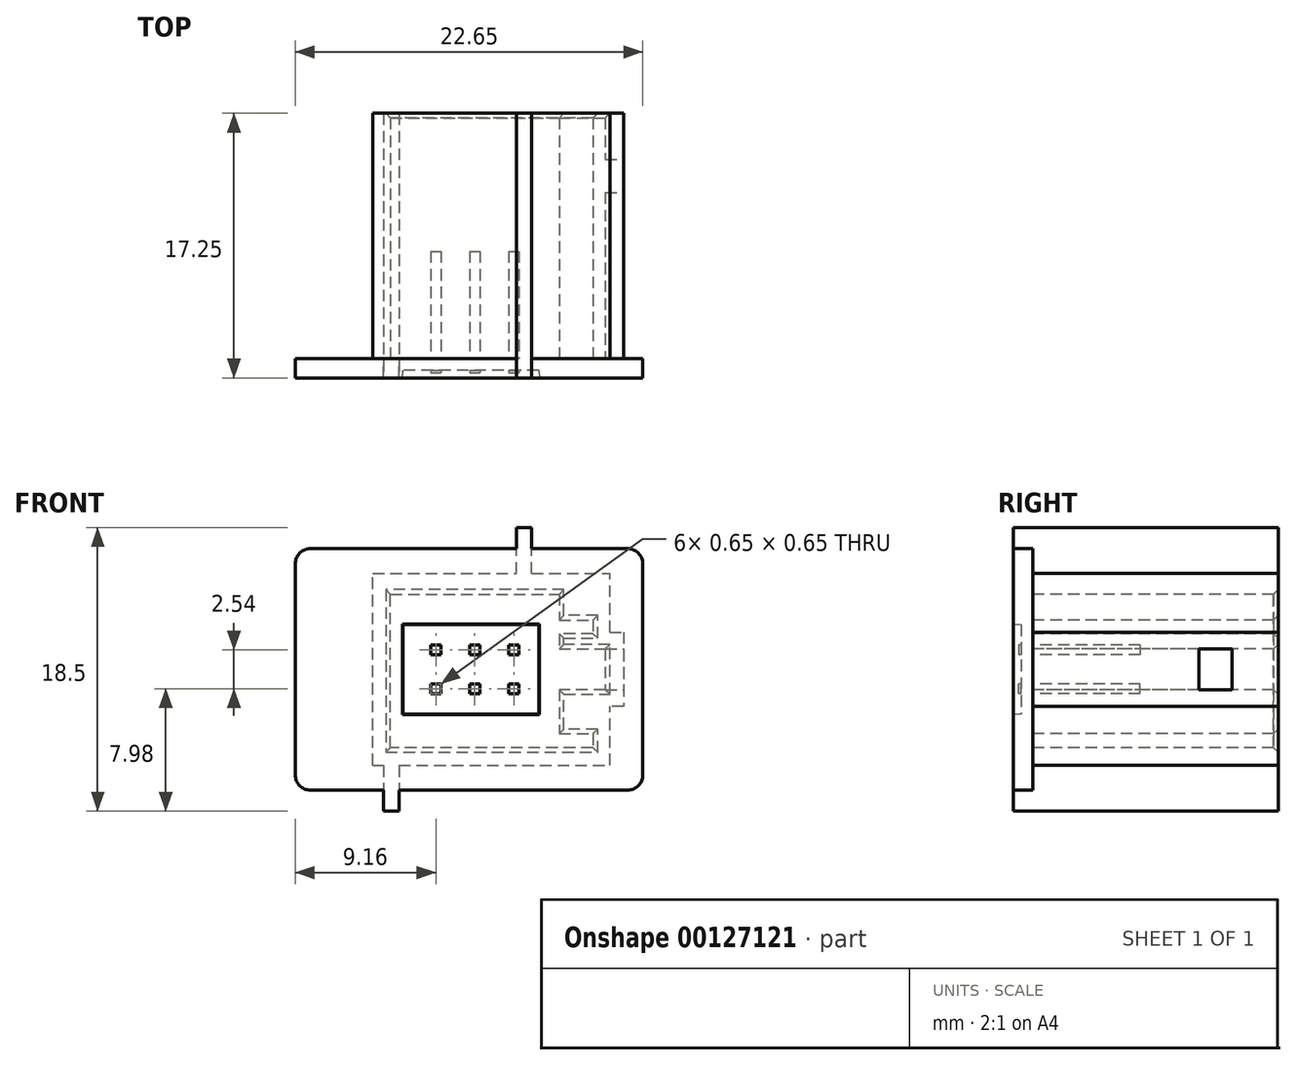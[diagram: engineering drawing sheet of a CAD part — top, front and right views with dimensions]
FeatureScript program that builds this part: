
annotation { "Feature Type Name" : "Feature", "Feature Type Description" : "" }
export const myFeature = defineFeature(function(context is Context, id is Id, definition is map)
    precondition{}
    {
        {
            var Q0;
            Q0=qCreatedBy(makeId("Front.planeOp"),FACE);
            var sketch = newSketch(context, id + "F0", { "sketchPlane" : qUnion([Q0])});
            skLineSegment(sketch, "E0", {"start": v(0, 0) * mm, "end": v(0, 10) * mm});
            skLineSegment(sketch, "E1", {"start": v(0, 10) * mm, "end": v(11, 10) * mm});
            skLineSegment(sketch, "E2", {"start": v(13.2, 8.32) * mm, "end": v(13.2, 7.42) * mm});
            skLineSegment(sketch, "E3", {"start": v(13.2, 7.42) * mm, "end": v(11, 7.42) * mm});
            skLineSegment(sketch, "E4", {"start": v(11, 7.42) * mm, "end": v(11, 6.42) * mm});
            skLineSegment(sketch, "E5", {"start": v(11, 6.42) * mm, "end": v(14, 6.42) * mm});
            skLineSegment(sketch, "E6", {"start": v(14, 6.43) * mm, "end": v(14, 3.77) * mm});
            skLineSegment(sketch, "E7", {"start": v(14, 3.77) * mm, "end": v(11, 3.77) * mm});
            skLineSegment(sketch, "E8", {"start": v(11, 3.77) * mm, "end": v(11, 0.9) * mm});
            skLineSegment(sketch, "E9", {"start": v(11, 0.9) * mm, "end": v(13.2, 0.9) * mm});
            skLineSegment(sketch, "E10", {"start": v(13.2, 0.9) * mm, "end": v(13.2, 0) * mm});
            skLineSegment(sketch, "E11", {"start": v(13.2, 0) * mm, "end": v(0, 0) * mm});
            skLineSegment(sketch, "E12.bottom", {"start": v(-1.15, -1.15) * mm, "end": v(-0.45, -1.15) * mm});
            skLineSegment(sketch, "E12.top", {"start": v(-1.15, 11.35) * mm, "end": v(8.2, 11.35) * mm});
            skLineSegment(sketch, "E12.left", {"start": v(-1.15, -1.15) * mm, "end": v(-1.15, 11.35) * mm});
            skLineSegment(sketch, "E12.right", {"start": v(14.3, -1.15) * mm, "end": v(14.3, 2.68) * mm});
            skLineSegment(sketch, "E13", {"start": v(14.3, 7.53) * mm, "end": v(15.2, 7.53) * mm});
            skLineSegment(sketch, "E14", {"start": v(15.2, 7.53) * mm, "end": v(15.2, 2.68) * mm});
            skLineSegment(sketch, "E15", {"start": v(15.2, 2.68) * mm, "end": v(14.3, 2.68) * mm});
            skLineSegment(sketch, "E16.top", {"start": v(8.2, 14.35) * mm, "end": v(9.2, 14.35) * mm});
            skLineSegment(sketch, "E16.left", {"start": v(8.2, 11.35) * mm, "end": v(8.2, 14.35) * mm});
            skLineSegment(sketch, "E16.right", {"start": v(9.2, 11.35) * mm, "end": v(9.2, 14.35) * mm});
            skLineSegment(sketch, "E17.top", {"start": v(0.55, -4.15) * mm, "end": v(-0.45, -4.15) * mm});
            skLineSegment(sketch, "E17.left", {"start": v(0.55, -1.15) * mm, "end": v(0.55, -4.15) * mm});
            skLineSegment(sketch, "E17.right", {"start": v(-0.45, -1.15) * mm, "end": v(-0.45, -4.15) * mm});
            skLineSegment(sketch, "E18.trimOffspring", {"start": v(9.2, 11.35) * mm, "end": v(14.3, 11.35) * mm});
            skLineSegment(sketch, "E19.trimOffspring", {"start": v(0.55, -1.15) * mm, "end": v(14.3, -1.15) * mm});
            skLineSegment(sketch, "E20.trimOffspring", {"start": v(14.3, 7.53) * mm, "end": v(14.3, 11.35) * mm});
            skLineSegment(sketch, "E21", {"start": v(15.2, 5.1) * mm, "end": v(-1.15, 5.1) * mm, "construction": true});
            skPoint(sketch, "E22", {"position": v(14, 5.1) * mm});
            skLineSegment(sketch, "E23.bottom", {"start": v(-6.2, 12.97) * mm, "end": v(16.45, 12.97) * mm});
            skLineSegment(sketch, "E23.top", {"start": v(-6.2, -2.78) * mm, "end": v(16.45, -2.78) * mm});
            skLineSegment(sketch, "E23.left", {"start": v(-6.2, 12.97) * mm, "end": v(-6.2, -2.77) * mm});
            skLineSegment(sketch, "E23.right", {"start": v(16.45, 12.97) * mm, "end": v(16.45, -2.78) * mm});
            skLineSegment(sketch, "E24", {"start": v(15.2, 5.1) * mm, "end": v(16.45, 5.1) * mm, "construction": true});
            skLineSegment(sketch, "E25.bottom", {"start": v(2.63, 6.7) * mm, "end": v(3.28, 6.7) * mm});
            skLineSegment(sketch, "E25.top", {"start": v(2.63, 6.05) * mm, "end": v(3.28, 6.05) * mm});
            skLineSegment(sketch, "E25.left", {"start": v(2.63, 6.7) * mm, "end": v(2.63, 6.04) * mm});
            skLineSegment(sketch, "E25.right", {"start": v(3.28, 6.7) * mm, "end": v(3.28, 6.05) * mm});
            skPoint(sketch, "E26", {"position": v(2.63, 6.37) * mm});
            skLineSegment(sketch, "E27.1.0.0", {"start": v(5.17, 6.05) * mm, "end": v(5.82, 6.05) * mm});
            skLineSegment(sketch, "E27.1.0.1", {"start": v(5.17, 6.7) * mm, "end": v(5.17, 6.04) * mm});
            skLineSegment(sketch, "E27.1.0.2", {"start": v(5.17, 6.7) * mm, "end": v(5.82, 6.7) * mm});
            skLineSegment(sketch, "E27.1.0.3", {"start": v(5.82, 6.7) * mm, "end": v(5.82, 6.05) * mm});
            skLineSegment(sketch, "E27.2.0.0", {"start": v(7.71, 6.05) * mm, "end": v(8.36, 6.05) * mm});
            skLineSegment(sketch, "E27.2.0.1", {"start": v(7.71, 6.7) * mm, "end": v(7.71, 6.04) * mm});
            skLineSegment(sketch, "E27.2.0.2", {"start": v(7.71, 6.7) * mm, "end": v(8.36, 6.7) * mm});
            skLineSegment(sketch, "E27.2.0.3", {"start": v(8.36, 6.7) * mm, "end": v(8.36, 6.05) * mm});
            skLineSegment(sketch, "E27.direction1", {"start": v(3.28, 6.05) * mm, "end": v(5.82, 6.05) * mm, "construction": true});
            skLineSegment(sketch, "E28.MirrorCS", {"start": v(2.63, 4.16) * mm, "end": v(3.28, 4.16) * mm});
            skLineSegment(sketch, "E29.MirrorCS", {"start": v(2.63, 3.5) * mm, "end": v(2.63, 4.16) * mm});
            skLineSegment(sketch, "E30.MirrorCS", {"start": v(2.63, 3.5) * mm, "end": v(3.28, 3.5) * mm});
            skLineSegment(sketch, "E31.MirrorCS", {"start": v(3.28, 3.5) * mm, "end": v(3.28, 4.16) * mm});
            skLineSegment(sketch, "E32.1.0.0", {"start": v(5.17, 3.5) * mm, "end": v(5.83, 3.5) * mm});
            skLineSegment(sketch, "E32.1.0.1", {"start": v(5.83, 3.5) * mm, "end": v(5.83, 4.16) * mm});
            skLineSegment(sketch, "E32.1.0.2", {"start": v(5.17, 4.16) * mm, "end": v(5.82, 4.16) * mm});
            skLineSegment(sketch, "E32.1.0.3", {"start": v(5.17, 3.5) * mm, "end": v(5.17, 4.16) * mm});
            skLineSegment(sketch, "E32.2.0.0", {"start": v(7.71, 3.5) * mm, "end": v(8.36, 3.5) * mm});
            skLineSegment(sketch, "E32.2.0.1", {"start": v(8.36, 3.5) * mm, "end": v(8.36, 4.16) * mm});
            skLineSegment(sketch, "E32.2.0.2", {"start": v(7.71, 4.16) * mm, "end": v(8.36, 4.16) * mm});
            skLineSegment(sketch, "E32.2.0.3", {"start": v(7.71, 3.5) * mm, "end": v(7.71, 4.16) * mm});
            skLineSegment(sketch, "E32.direction1", {"start": v(3.28, 4.16) * mm, "end": v(5.82, 4.16) * mm, "construction": true});
            skLineSegment(sketch, "E33", {"start": v(5.5, 0) * mm, "end": v(5.5, 10) * mm, "construction": true});
            skPoint(sketch, "E34", {"position": v(5.5, 3.5) * mm});
            skLineSegment(sketch, "E35", {"start": v(11, 10) * mm, "end": v(11, 8.32) * mm});
            skLineSegment(sketch, "E36", {"start": v(11, 8.32) * mm, "end": v(13.2, 8.32) * mm});
            skSolve(sketch);
        }
        {
            var Q0;
            Q0=makeQuery(id+"F0.imprint","IMPRINT",FACE,{"disambiguationData":[TD([[makeQuery(id+"F0.imprint","IMPRINT",EDGE,{"derivedFrom":sQuery(id+"F0.wireOp",EDGE,"E0")}),1.0]])]});
            var Q1;
            {var subQ0=sQuery(id+"F0.wireOp",EDGE,"E16.top");Q1=makeQuery(id+"F0.imprint","IMPRINT",FACE,{"disambiguationData":[TD([[makeQuery(id+"F0.imprint","IMPRINT",EDGE,{"derivedFrom":subQ0}),-1.0]])]});}
            var Q2;
            {var subQ0=sQuery(id+"F0.wireOp",EDGE,"E17.top");Q2=makeQuery(id+"F0.imprint","IMPRINT",FACE,{"disambiguationData":[TD([[makeQuery(id+"F0.imprint","IMPRINT",EDGE,{"derivedFrom":subQ0}),-1.0]])]});}
            extrude(context, id + "F1", {"entities" : qUnion([Q0, Q1, Q2]), "oppositeDirection" : true, "depth" : 16 * mm});
        }
        {
            var Q0;
            Q0 = qSketchRegion(id + "F0", true);
            var Q1;
            Q1=makeQuery(id+"F0.imprint","IMPRINT",FACE,{"disambiguationData":[TD([[makeQuery(id+"F0.imprint","IMPRINT",EDGE,{"derivedFrom":sQuery(id+"F0.wireOp",EDGE,"E0")}),-1.0]])]});
            extrude(context, id + "F2", {"entities" : qUnion([Q0, Q1]), "operationType" : NewBodyOperationType.ADD, "depth" : 1.25 * mm});
        }
        {
            var Q0;
            Q0=makeQuery(id+"F1.opExtrude","SWEPT_FACE",FACE,{"disambiguationData":[OSD([sQuery(id+"F0.wireOp",EDGE,"E14")])]});
            var sketch = newSketch(context, id + "F3", { "sketchPlane" : qUnion([Q0])});
            skLineSegment(sketch, "E37.bottom", {"start": v(10.85, 6.42) * mm, "end": v(13, 6.42) * mm});
            skLineSegment(sketch, "E37.top", {"start": v(10.85, 3.77) * mm, "end": v(13, 3.77) * mm});
            skLineSegment(sketch, "E37.left", {"start": v(10.85, 6.42) * mm, "end": v(10.85, 3.77) * mm});
            skLineSegment(sketch, "E37.right", {"start": v(13, 6.42) * mm, "end": v(13, 3.77) * mm});
            skLineSegment(sketch, "E38", {"start": v(16, 5.1) * mm, "end": v(0, 5.1) * mm, "construction": true});
            skPoint(sketch, "E39", {"position": v(13, 5.1) * mm});
            skLineSegment(sketch, "E40.0", {"start": v(16, 3.77) * mm, "end": v(0, 3.77) * mm, "construction": true});
            skSolve(sketch);
        }
        {
            var Q0;
            Q0=makeQuery(id+"F3.imprint","IMPRINT",FACE,{"disambiguationData":[TD([[makeQuery(id+"F3.imprint","IMPRINT",EDGE,{"derivedFrom":sQuery(id+"F3.wireOp",EDGE,"E37.bottom")}),-1.0]])]});
            var Q1;
            Q1=makeQuery(id+"F1.opExtrude","SWEPT_FACE",FACE,{"disambiguationData":[OSD([sQuery(id+"F0.wireOp",EDGE,"E6")])]});
            extrude(context, id + "F4", {"entities" : qUnion([Q0]), "operationType" : NewBodyOperationType.REMOVE, "endBound" : BoundingType.UP_TO_SURFACE, "oppositeDirection" : true, "endBoundEntityFace" : qUnion([Q1]), "depth" : 25 * mm});
        }
        {
            var Q0;
            Q0=makeQuery(id+"F2.opExtrude","SWEPT_EDGE",EDGE,{"disambiguationData":[OSD([sQuery(id+"F0.wireOp",EDGE,"E23.bottom"),sQuery(id+"F0.wireOp",EDGE,"E23.right")])]});
            var Q1;
            Q1=makeQuery(id+"F2.opExtrude","SWEPT_EDGE",EDGE,{"disambiguationData":[OSD([sQuery(id+"F0.wireOp",EDGE,"E23.bottom"),sQuery(id+"F0.wireOp",EDGE,"E23.left")])]});
            var Q2;
            Q2=makeQuery(id+"F2.opExtrude","SWEPT_EDGE",EDGE,{"disambiguationData":[OSD([sQuery(id+"F0.wireOp",EDGE,"E23.top"),sQuery(id+"F0.wireOp",EDGE,"E23.right")])]});
            var Q3;
            Q3=makeQuery(id+"F2.opExtrude","SWEPT_EDGE",EDGE,{"disambiguationData":[OSD([sQuery(id+"F0.wireOp",EDGE,"E23.top"),sQuery(id+"F0.wireOp",EDGE,"E23.left")])]});
            fillet(context, id + "F5", {"entities" : qUnion([Q0, Q1, Q2, Q3]), "radius" : 1 * mm, "tangentPropagation" : true, "allowEdgeOverflow" : false});
        }
        {
            var Q0;
            Q0=makeQuery(id+"F2.opExtrude","CAP_FACE",FACE,{"disambiguationData":[OSD([sQuery(id+"F0.wireOp",EDGE,"E16.top"),sQuery(id+"F0.wireOp",EDGE,"E16.left"),sQuery(id+"F0.wireOp",EDGE,"E16.right"),sQuery(id+"F0.wireOp",EDGE,"E17.top"),sQuery(id+"F0.wireOp",EDGE,"E17.left"),sQuery(id+"F0.wireOp",EDGE,"E17.right"),sQuery(id+"F0.wireOp",EDGE,"E23.bottom"),sQuery(id+"F0.wireOp",EDGE,"E23.top"),sQuery(id+"F0.wireOp",EDGE,"E23.left"),sQuery(id+"F0.wireOp",EDGE,"E23.right")])],"isStart":false});
            var sketch = newSketch(context, id + "F6", { "sketchPlane" : qUnion([Q0])});
            skLineSegment(sketch, "E41.bottom", {"start": v(0.8, 8.05) * mm, "end": v(9.7, 8.05) * mm});
            skLineSegment(sketch, "E41.top", {"start": v(0.8, 2.15) * mm, "end": v(9.7, 2.15) * mm});
            skLineSegment(sketch, "E41.left", {"start": v(0.8, 8.05) * mm, "end": v(0.8, 2.15) * mm});
            skLineSegment(sketch, "E41.right", {"start": v(9.7, 8.05) * mm, "end": v(9.7, 2.15) * mm});
            skLineSegment(sketch, "E42", {"start": v(0.8, 5.1) * mm, "end": v(-6.2, 5.1) * mm, "construction": true});
            skSolve(sketch);
        }
        {
            var Q0;
            Q0 = qSketchRegion(id + "F6", true);
            extrude(context, id + "F7", {"entities" : qUnion([Q0]), "operationType" : NewBodyOperationType.REMOVE, "oppositeDirection" : true, "depth" : 0.5 * mm, "hasDraft" : true, "draftAngle" : 3 * degree, "draftPullDirection" : true});
        }
        {
            var Q0;
            Q0=makeQuery(id+"F0.imprint","IMPRINT",FACE,{"disambiguationData":[TD([[makeQuery(id+"F0.imprint","IMPRINT",EDGE,{"derivedFrom":sQuery(id+"F0.wireOp",EDGE,"E25.bottom")}),-1.0]])]});
            var Q1;
            Q1=makeQuery(id+"F0.imprint","IMPRINT",FACE,{"disambiguationData":[TD([[makeQuery(id+"F0.imprint","IMPRINT",EDGE,{"derivedFrom":sQuery(id+"F0.wireOp",EDGE,"E27.1.0.0")}),1.0]])]});
            var Q2;
            Q2=makeQuery(id+"F0.imprint","IMPRINT",FACE,{"disambiguationData":[TD([[makeQuery(id+"F0.imprint","IMPRINT",EDGE,{"derivedFrom":sQuery(id+"F0.wireOp",EDGE,"E27.2.0.0")}),1.0]])]});
            var Q3;
            Q3=makeQuery(id+"F0.imprint","IMPRINT",FACE,{"disambiguationData":[TD([[makeQuery(id+"F0.imprint","IMPRINT",EDGE,{"derivedFrom":sQuery(id+"F0.wireOp",EDGE,"E28.MirrorCS")}),-1.0]])]});
            var Q4;
            Q4=makeQuery(id+"F0.imprint","IMPRINT",FACE,{"disambiguationData":[TD([[makeQuery(id+"F0.imprint","IMPRINT",EDGE,{"derivedFrom":sQuery(id+"F0.wireOp",EDGE,"E32.1.0.0")}),1.0]])]});
            var Q5;
            Q5=makeQuery(id+"F0.imprint","IMPRINT",FACE,{"disambiguationData":[TD([[makeQuery(id+"F0.imprint","IMPRINT",EDGE,{"derivedFrom":sQuery(id+"F0.wireOp",EDGE,"E32.2.0.0")}),1.0]])]});
            extrude(context, id + "F8", {"entities" : qUnion([Q0, Q1, Q2, Q3, Q4, Q5]), "operationType" : NewBodyOperationType.ADD, "oppositeDirection" : true, "depth" : 7 * mm, "hasSecondDirection" : true, "secondDirectionOppositeDirection" : false, "secondDirectionDepth" : 0.9 * mm});
        }
        {
            var Q0;
            Q0=makeQuery(id+"F1.opExtrude","CAP_EDGE",EDGE,{"disambiguationData":[OSD([sQuery(id+"F0.wireOp",EDGE,"E3")])],"isStart":false});
            var Q1;
            Q1=makeQuery(id+"F1.opExtrude","CAP_EDGE",EDGE,{"disambiguationData":[OSD([sQuery(id+"F0.wireOp",EDGE,"E2")])],"isStart":false});
            var Q2;
            Q2=makeQuery(id+"F1.opExtrude","CAP_EDGE",EDGE,{"disambiguationData":[OSD([sQuery(id+"F0.wireOp",EDGE,"E1")])],"isStart":false});
            var Q3;
            Q3=makeQuery(id+"F1.opExtrude","CAP_EDGE",EDGE,{"disambiguationData":[OSD([sQuery(id+"F0.wireOp",EDGE,"E0")])],"isStart":false});
            var Q4;
            Q4=makeQuery(id+"F1.opExtrude","CAP_EDGE",EDGE,{"disambiguationData":[OSD([sQuery(id+"F0.wireOp",EDGE,"E11")])],"isStart":false});
            var Q5;
            Q5=makeQuery(id+"F1.opExtrude","CAP_EDGE",EDGE,{"disambiguationData":[OSD([sQuery(id+"F0.wireOp",EDGE,"VaUyXeas-xeOn-mh1J-bfMQ-0cuGWoMnUsml")])],"isStart":false});
            var Q6;
            Q6=makeQuery(id+"F1.opExtrude","CAP_EDGE",EDGE,{"disambiguationData":[OSD([sQuery(id+"F0.wireOp",EDGE,"K3pJPl0Y-jdtS-PQSX-VIi2-gQ6Jj0WlDIje")])],"isStart":false});
            var Q7;
            Q7=makeQuery(id+"F1.opExtrude","CAP_EDGE",EDGE,{"disambiguationData":[OSD([sQuery(id+"F0.wireOp",EDGE,"E9")])],"isStart":false});
            var Q8;
            Q8=makeQuery(id+"F1.opExtrude","CAP_EDGE",EDGE,{"disambiguationData":[OSD([sQuery(id+"F0.wireOp",EDGE,"E10")])],"isStart":false});
            var Q9;
            Q9=makeQuery(id+"F1.opExtrude","CAP_EDGE",EDGE,{"disambiguationData":[OSD([sQuery(id+"F0.wireOp",EDGE,"E8")])],"isStart":false});
            var Q10;
            Q10=makeQuery(id+"F1.opExtrude","CAP_EDGE",EDGE,{"disambiguationData":[OSD([sQuery(id+"F0.wireOp",EDGE,"E7")])],"isStart":false});
            var Q11;
            Q11=makeQuery(id+"F1.opExtrude","CAP_EDGE",EDGE,{"disambiguationData":[OSD([sQuery(id+"F0.wireOp",EDGE,"E6")])],"isStart":false});
            var Q12;
            Q12=makeQuery(id+"F1.opExtrude","CAP_EDGE",EDGE,{"disambiguationData":[OSD([sQuery(id+"F0.wireOp",EDGE,"E5")])],"isStart":false});
            var Q13;
            Q13=makeQuery(id+"F1.opExtrude","CAP_EDGE",EDGE,{"disambiguationData":[OSD([sQuery(id+"F0.wireOp",EDGE,"E4")])],"isStart":false});
            var Q14;
            Q14=makeQuery(id+"F1.opExtrude","CAP_EDGE",EDGE,{"disambiguationData":[OSD([sQuery(id+"F0.wireOp",EDGE,"E36")])],"isStart":false});
            var Q15;
            Q15=makeQuery(id+"F1.opExtrude","CAP_EDGE",EDGE,{"disambiguationData":[OSD([sQuery(id+"F0.wireOp",EDGE,"E35")])],"isStart":false});
            chamfer(context, id + "F9", {"entities" : qUnion([Q0, Q1, Q2, Q3, Q4, Q5, Q6, Q7, Q8, Q9, Q10, Q11, Q12, Q13, Q14, Q15]), "width" : 0.3 * mm, "tangentPropagation" : true});
        }
    });
